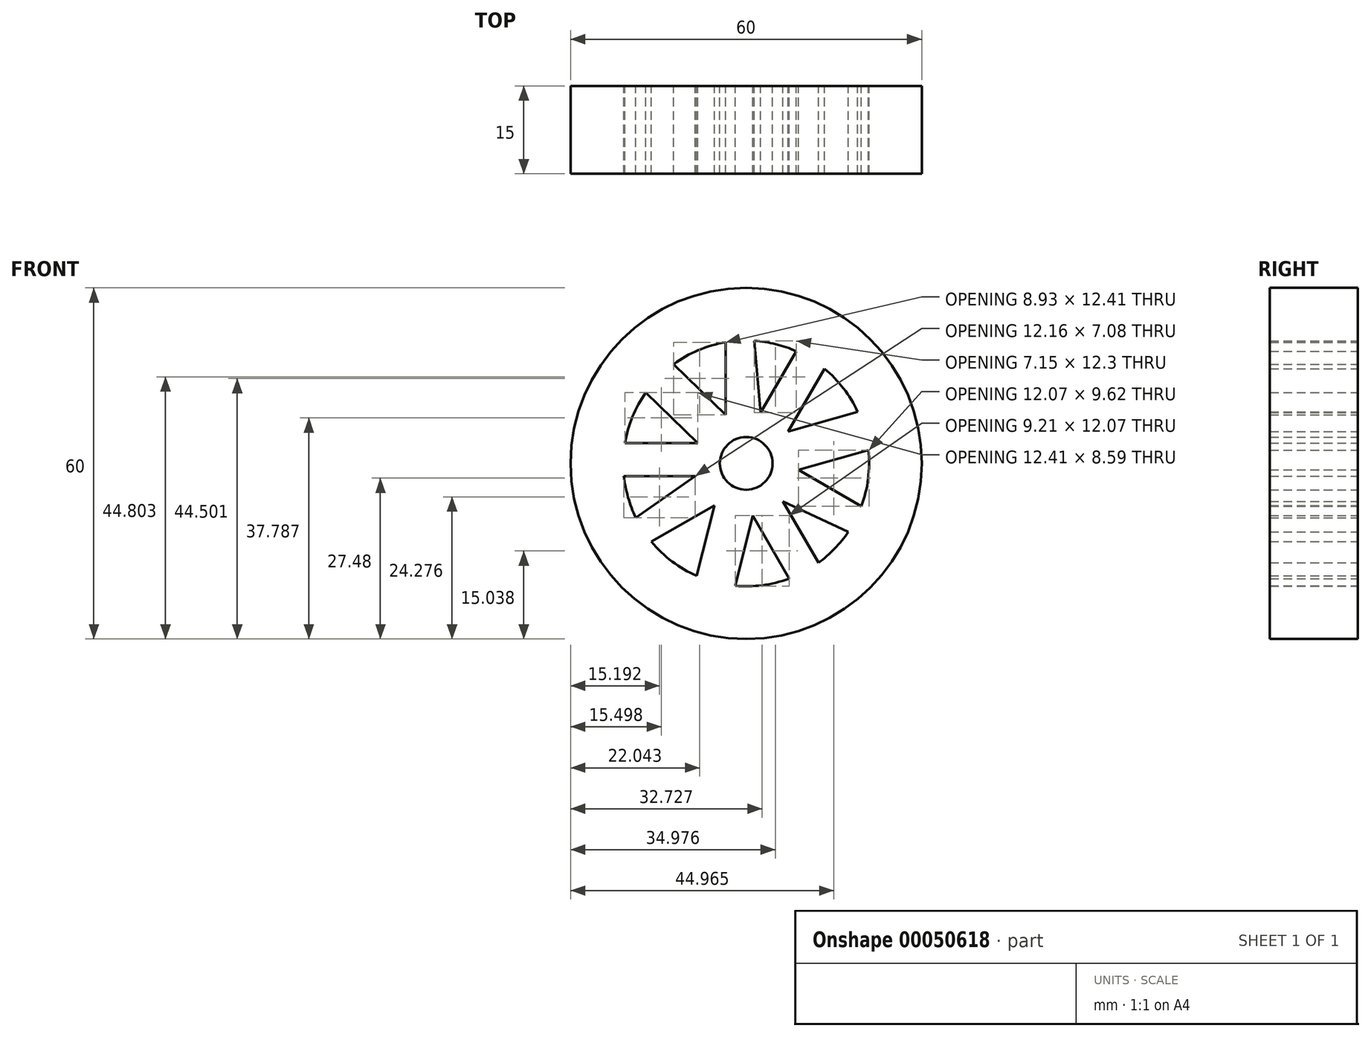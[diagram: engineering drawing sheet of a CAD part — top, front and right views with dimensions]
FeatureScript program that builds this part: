
annotation { "Feature Type Name" : "Feature", "Feature Type Description" : "" }
export const myFeature = defineFeature(function(context is Context, id is Id, definition is map)
    precondition{}
    {
        {
            var Q0;
            Q0=qCreatedBy(makeId("Front.planeOp"),FACE);
            var sketch = newSketch(context, id + "F0", { "sketchPlane" : qUnion([Q0])});
            skCircle(sketch, "E0", {"center": v(0, 0) * mm, "radius": 30 * mm});
            skArc(sketch, "E1", {"start": v(-3.5, 20.7) * mm, "mid": v(-8.18, 19.34) * mm, "end": v(-12.42, 16.93) * mm});
            skLineSegment(sketch, "E2", {"start": v(-3.5, 8.3) * mm, "end": v(-3.5, 8.3) * mm});
            skCircle(sketch, "E3", {"center": v(0, 0) * mm, "radius": 4.5 * mm});
            skLineSegment(sketch, "E4.0", {"start": v(-3.5, 30) * mm, "end": v(-3.5, 29.8) * mm});
            skLineSegment(sketch, "E5.0", {"start": v(0.62, 30) * mm, "end": v(0.64, 29.77) * mm});
            skLineSegment(sketch, "E6.trimOffspring", {"start": v(-3.5, 20.7) * mm, "end": v(-3.5, 8.3) * mm});
            skLineSegment(sketch, "E7.trimOffspring", {"start": v(1.4, 20.95) * mm, "end": v(2.47, 8.65) * mm});
            skLineSegment(sketch, "E8.trimOffspring", {"start": v(-8.3, 3.49) * mm, "end": v(-20.7, 3.49) * mm});
            skLineSegment(sketch, "E9.trimOffspring", {"start": v(-8.73, -2.19) * mm, "end": v(-20.89, -2.19) * mm});
            skLineSegment(sketch, "E10.trimOffspring", {"start": v(-29.8, 3.49) * mm, "end": v(-30, 3.49) * mm});
            skLineSegment(sketch, "E11.trimOffspring", {"start": v(-29.92, -2.19) * mm, "end": v(-30, -2.19) * mm});
            skLineSegment(sketch, "E12.1.0", {"start": v(-16.19, -13.38) * mm, "end": v(-5.44, -7.17) * mm});
            skLineSegment(sketch, "E12.1.1", {"start": v(-18.85, -9.26) * mm, "end": v(-8.73, -2.19) * mm});
            skLineSegment(sketch, "E12.1.2", {"start": v(1.13, -8.93) * mm, "end": v(7.33, -19.68) * mm});
            skLineSegment(sketch, "E12.1.3", {"start": v(6.26, -6.47) * mm, "end": v(12.34, -17) * mm});
            skLineSegment(sketch, "E12.2.0", {"start": v(19.68, -7.33) * mm, "end": v(8.93, -1.12) * mm});
            skLineSegment(sketch, "E12.2.1", {"start": v(17.44, -11.7) * mm, "end": v(6.26, -6.47) * mm});
            skLineSegment(sketch, "E12.2.2", {"start": v(7.17, 5.44) * mm, "end": v(13.38, 16.19) * mm});
            skLineSegment(sketch, "E12.2.3", {"start": v(2.47, 8.65) * mm, "end": v(8.55, 19.18) * mm});
            skLineSegment(sketch, "E13.0", {"start": v(-23.82, 18.52) * mm, "end": v(-23.7, 18.4) * mm});
            skLineSegment(sketch, "E14.0", {"start": v(-19.1, 23.4) * mm, "end": v(-18.95, 23.26) * mm});
            skLineSegment(sketch, "E15.trimOffspring", {"start": v(-12.42, 16.93) * mm, "end": v(-3.5, 8.3) * mm});
            skLineSegment(sketch, "E16.trimOffspring", {"start": v(-17.17, 12.08) * mm, "end": v(-8.3, 3.49) * mm});
            skLineSegment(sketch, "E17.1.0", {"start": v(-8.46, -19.22) * mm, "end": v(-5.44, -7.17) * mm});
            skLineSegment(sketch, "E17.1.1", {"start": v(-1.88, -20.92) * mm, "end": v(1.13, -8.93) * mm});
            skLineSegment(sketch, "E17.2.0", {"start": v(20.87, 2.29) * mm, "end": v(8.93, -1.12) * mm});
            skLineSegment(sketch, "E17.2.1", {"start": v(19.05, 8.83) * mm, "end": v(7.17, 5.44) * mm});
            skArc(sketch, "E18.trimOffspring", {"start": v(-17.17, 12.08) * mm, "mid": v(-19.42, 7.98) * mm, "end": v(-20.7, 3.49) * mm});
            skLineSegment(sketch, "E19.trimOffspring", {"start": v(-8.3, 3.49) * mm, "end": v(-8.3, 3.49) * mm});
            skLineSegment(sketch, "E20.trimOffspring", {"start": v(-8.73, -2.19) * mm, "end": v(-8.73, -2.19) * mm});
            skArc(sketch, "E21.trimOffspring", {"start": v(-20.89, -2.19) * mm, "mid": v(-20.18, -5.81) * mm, "end": v(-18.85, -9.26) * mm});
            skArc(sketch, "E22.trimOffspring", {"start": v(-16.19, -13.38) * mm, "mid": v(-12.66, -16.75) * mm, "end": v(-8.46, -19.22) * mm});
            skLineSegment(sketch, "E23.trimOffspring", {"start": v(-5.44, -7.17) * mm, "end": v(-5.44, -7.17) * mm});
            skLineSegment(sketch, "E24.trimOffspring", {"start": v(1.13, -8.93) * mm, "end": v(1.13, -8.93) * mm});
            skArc(sketch, "E25.trimOffspring", {"start": v(-1.88, -20.92) * mm, "mid": v(2.8, -20.81) * mm, "end": v(7.33, -19.68) * mm});
            skLineSegment(sketch, "E26.trimOffspring", {"start": v(6.26, -6.47) * mm, "end": v(6.26, -6.47) * mm});
            skArc(sketch, "E27.trimOffspring", {"start": v(12.34, -17) * mm, "mid": v(15.12, -14.57) * mm, "end": v(17.44, -11.7) * mm});
            skLineSegment(sketch, "E28.trimOffspring", {"start": v(8.93, -1.12) * mm, "end": v(8.93, -1.12) * mm});
            skArc(sketch, "E29.trimOffspring", {"start": v(19.68, -7.33) * mm, "mid": v(20.84, -2.59) * mm, "end": v(20.87, 2.29) * mm});
            skLineSegment(sketch, "E30.trimOffspring", {"start": v(7.17, 5.44) * mm, "end": v(7.17, 5.44) * mm});
            skArc(sketch, "E31.trimOffspring", {"start": v(19.05, 8.83) * mm, "mid": v(16.63, 12.83) * mm, "end": v(13.38, 16.19) * mm});
            skLineSegment(sketch, "E32.trimOffspring", {"start": v(2.47, 8.65) * mm, "end": v(2.47, 8.65) * mm});
            skArc(sketch, "E33.trimOffspring", {"start": v(8.55, 19.18) * mm, "mid": v(5.05, 20.38) * mm, "end": v(1.4, 20.95) * mm});
            skSolve(sketch);
        }
        {
            var Q0;
            Q0=makeQuery(id+"F0.imprint","IMPRINT",FACE,{"disambiguationData":[TD([[makeQuery(id+"F0.imprint","IMPRINT",EDGE,{"derivedFrom":sQuery(id+"F0.wireOp",EDGE,"E1")}),-1.0]])]});
            extrude(context, id + "F1", {"entities" : qUnion([Q0]), "endBound" : BoundingType.SYMMETRIC, "depth" : 15 * mm});
        }
    });
